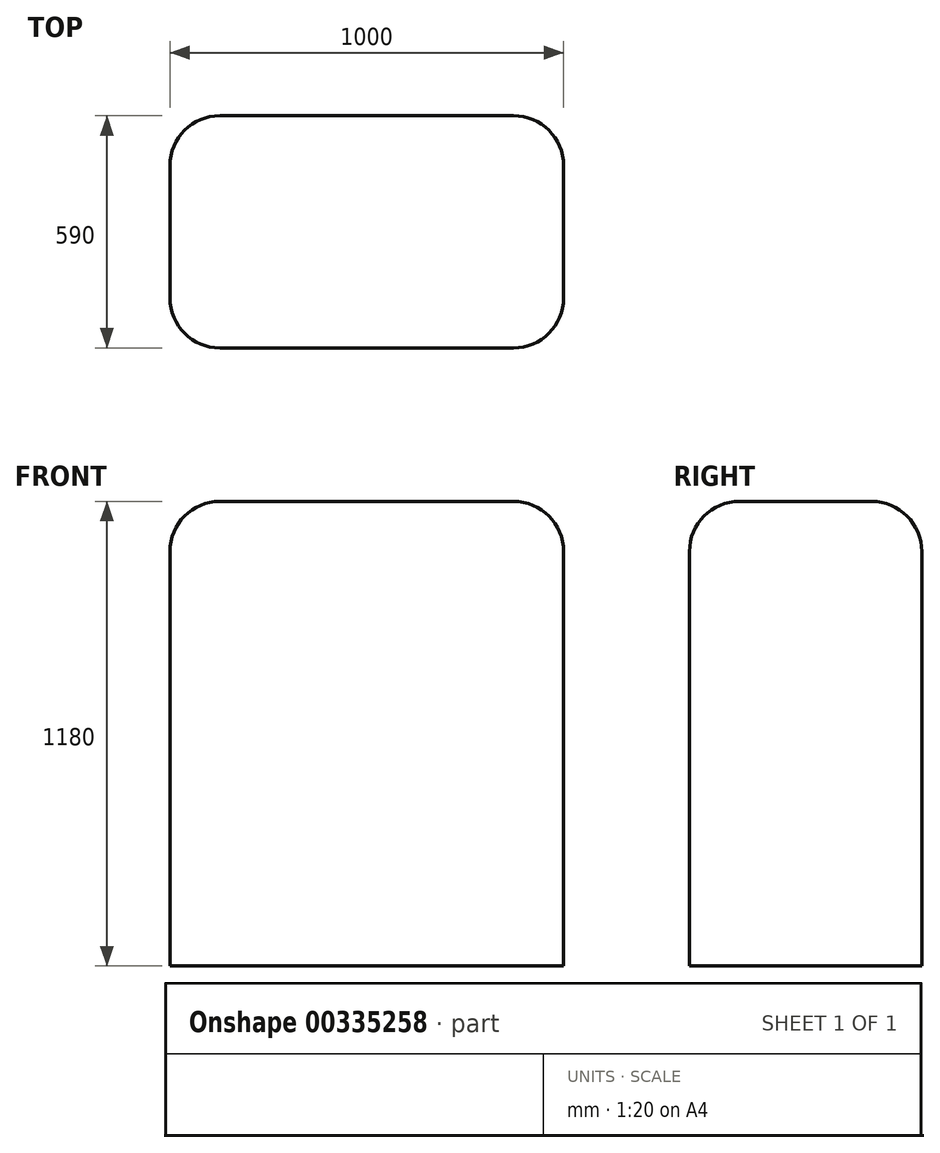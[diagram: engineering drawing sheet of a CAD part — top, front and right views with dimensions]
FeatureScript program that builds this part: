
annotation { "Feature Type Name" : "Feature", "Feature Type Description" : "" }
export const myFeature = defineFeature(function(context is Context, id is Id, definition is map)
    precondition{}
    {
        {
            var Q0;
            Q0=qCreatedBy(makeId("Top.planeOp"),FACE);
            var sketch = newSketch(context, id + "F0", { "sketchPlane" : qUnion([Q0])});
            skLineSegment(sketch, "E0.bottom", {"start": v(500, 295) * mm, "end": v(-500, 295) * mm});
            skLineSegment(sketch, "E0.top", {"start": v(500, -295) * mm, "end": v(-500, -295) * mm});
            skLineSegment(sketch, "E0.left", {"start": v(500, 295) * mm, "end": v(500, -295) * mm});
            skLineSegment(sketch, "E0.right", {"start": v(-500, 295) * mm, "end": v(-500, -295) * mm});
            skPoint(sketch, "E0.middle", {"position": v(0, 0) * mm});
            skSolve(sketch);
        }
        {
            var Q0;
            Q0=makeQuery(id+"F0.imprint","IMPRINT",FACE,{"disambiguationData":[TD([[makeQuery(id+"F0.imprint","IMPRINT",EDGE,{"derivedFrom":sQuery(id+"F0.wireOp",EDGE,"E0.bottom")}),1.0]])]});
            extrude(context, id + "F1", {"entities" : qUnion([Q0]), "endBound" : BoundingType.SYMMETRIC, "depth" : 1180 * mm});
        }
        {
            var Q0;
            Q0=makeQuery(id+"F1.opExtrude","SWEPT_EDGE",EDGE,{"disambiguationData":[OSD([sQuery(id+"F0.wireOp",EDGE,"E0.top"),sQuery(id+"F0.wireOp",EDGE,"E0.right")])]});
            var Q1;
            Q1=makeQuery(id+"F1.opExtrude","CAP_EDGE",EDGE,{"disambiguationData":[OSD([sQuery(id+"F0.wireOp",EDGE,"E0.right")])],"isStart":false});
            var Q2;
            Q2=makeQuery(id+"F1.opExtrude","CAP_EDGE",EDGE,{"disambiguationData":[OSD([sQuery(id+"F0.wireOp",EDGE,"E0.top")])],"isStart":false});
            var Q3;
            Q3=makeQuery(id+"F1.opExtrude","CAP_EDGE",EDGE,{"disambiguationData":[OSD([sQuery(id+"F0.wireOp",EDGE,"E0.bottom")])],"isStart":false});
            var Q4;
            Q4=makeQuery(id+"F1.opExtrude","CAP_EDGE",EDGE,{"disambiguationData":[OSD([sQuery(id+"F0.wireOp",EDGE,"E0.left")])],"isStart":false});
            var Q5;
            Q5=makeQuery(id+"F1.opExtrude","SWEPT_EDGE",EDGE,{"disambiguationData":[OSD([sQuery(id+"F0.wireOp",EDGE,"E0.top"),sQuery(id+"F0.wireOp",EDGE,"E0.left")])]});
            var Q6;
            Q6=makeQuery(id+"F1.opExtrude","SWEPT_EDGE",EDGE,{"disambiguationData":[OSD([sQuery(id+"F0.wireOp",EDGE,"E0.bottom"),sQuery(id+"F0.wireOp",EDGE,"E0.left")])]});
            var Q7;
            Q7=makeQuery(id+"F1.opExtrude","SWEPT_EDGE",EDGE,{"disambiguationData":[OSD([sQuery(id+"F0.wireOp",EDGE,"E0.bottom"),sQuery(id+"F0.wireOp",EDGE,"E0.right")])]});
            fillet(context, id + "F2", {"entities" : qUnion([Q0, Q1, Q2, Q3, Q4, Q5, Q6, Q7]), "radius" : 127 * mm, "tangentPropagation" : true, "allowEdgeOverflow" : false});
        }
    });
